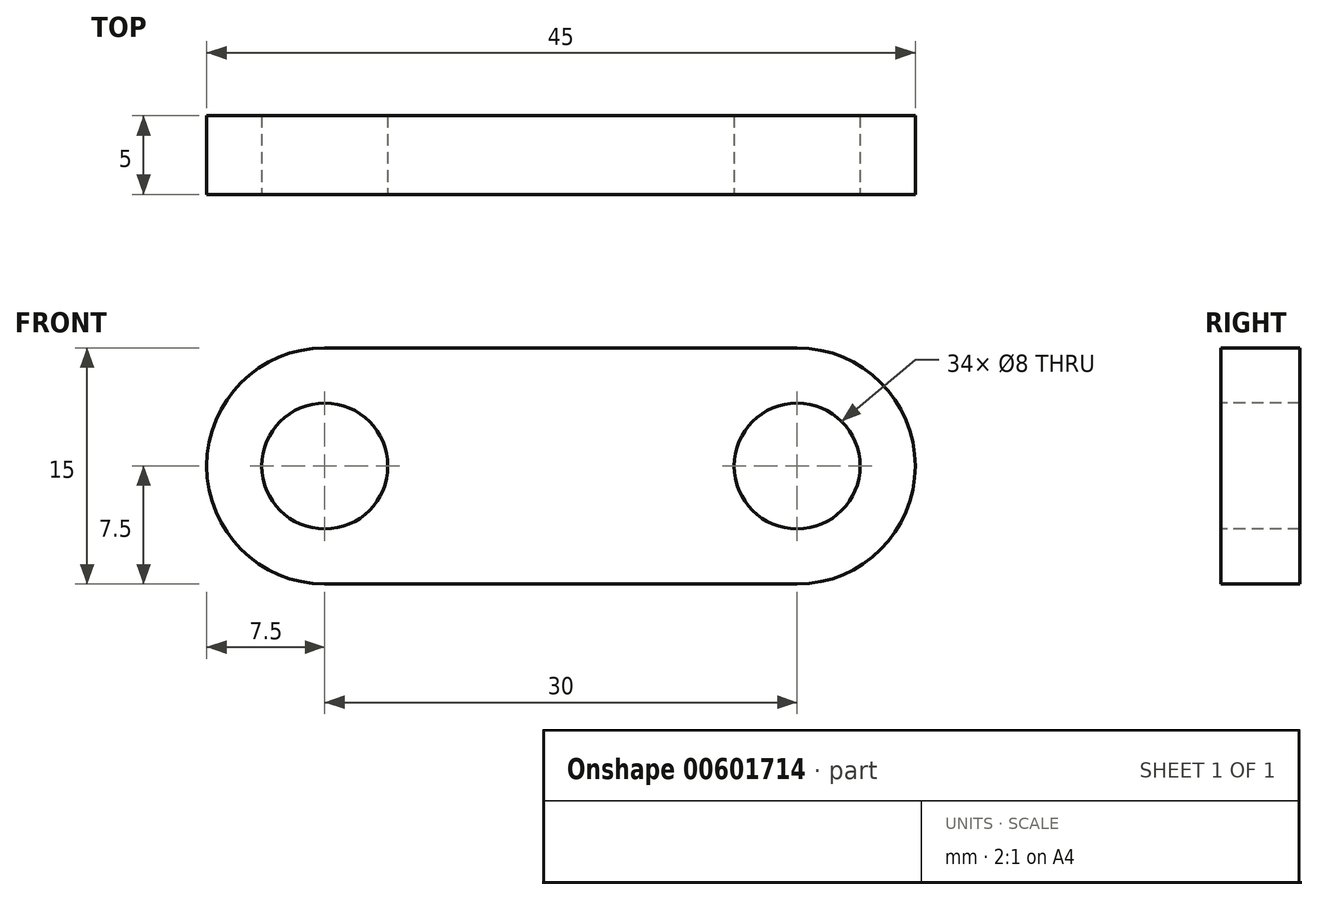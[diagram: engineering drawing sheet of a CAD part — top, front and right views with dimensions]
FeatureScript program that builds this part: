
annotation { "Feature Type Name" : "Feature", "Feature Type Description" : "" }
export const myFeature = defineFeature(function(context is Context, id is Id, definition is map)
    precondition{}
    {
        {
            var Q0;
            Q0=qCreatedBy(makeId("Front.planeOp"),FACE);
            var sketch = newSketch(context, id + "F0", { "sketchPlane" : qUnion([Q0])});
            skLineSegment(sketch, "E0", {"start": v(-15, 7.5) * mm, "end": v(15, 7.5) * mm});
            skLineSegment(sketch, "E1", {"start": v(-15, -7.5) * mm, "end": v(15, -7.5) * mm});
            skArc(sketch, "E2", {"start": v(15, -7.5) * mm, "mid": v(22.5, 0) * mm, "end": v(15, 7.5) * mm});
            skArc(sketch, "E3", {"start": v(-15, 7.5) * mm, "mid": v(-22.5, 0) * mm, "end": v(-15, -7.5) * mm});
            skSolve(sketch);
        }
        {
            var Q0;
            Q0=makeQuery(id+"F0.imprint","IMPRINT",FACE,{"disambiguationData":[TD([[makeQuery(id+"F0.imprint","IMPRINT",EDGE,{"derivedFrom":sQuery(id+"F0.wireOp",EDGE,"E0")}),-1.0]])]});
            extrude(context, id + "F1", {"entities" : qUnion([Q0]), "depth" : 5 * mm, "offsetDistance" : 25 * mm});
        }
        {
            var Q0;
            Q0=makeQuery(id+"F1.opExtrude","CAP_FACE",FACE,{"disambiguationData":[OSD([sQuery(id+"F0.wireOp",EDGE,"E0"),sQuery(id+"F0.wireOp",EDGE,"E1"),sQuery(id+"F0.wireOp",EDGE,"E2"),sQuery(id+"F0.wireOp",EDGE,"E3")])],"isStart":false});
            var sketch = newSketch(context, id + "F2", { "sketchPlane" : qUnion([Q0])});
            skCircle(sketch, "E4", {"center": v(15, 0) * mm, "radius": 4 * mm});
            skCircle(sketch, "E5", {"center": v(-15, 0) * mm, "radius": 4 * mm});
            skSolve(sketch);
        }
        {
            var Q0;
            Q0=makeQuery(id+"F2.imprint","IMPRINT",FACE,{"disambiguationData":[TD([[makeQuery(id+"F2.imprint","IMPRINT",EDGE,{"derivedFrom":sQuery(id+"F2.wireOp",EDGE,"E5")}),1.0]])]});
            var Q1;
            Q1=makeQuery(id+"F2.imprint","IMPRINT",FACE,{"disambiguationData":[TD([[makeQuery(id+"F2.imprint","IMPRINT",EDGE,{"derivedFrom":sQuery(id+"F2.wireOp",EDGE,"E4")}),1.0]])]});
            extrude(context, id + "F3", {"entities" : qUnion([Q0, Q1]), "operationType" : NewBodyOperationType.REMOVE, "oppositeDirection" : true, "depth" : 5 * mm, "offsetDistance" : 25 * mm});
        }
    });
